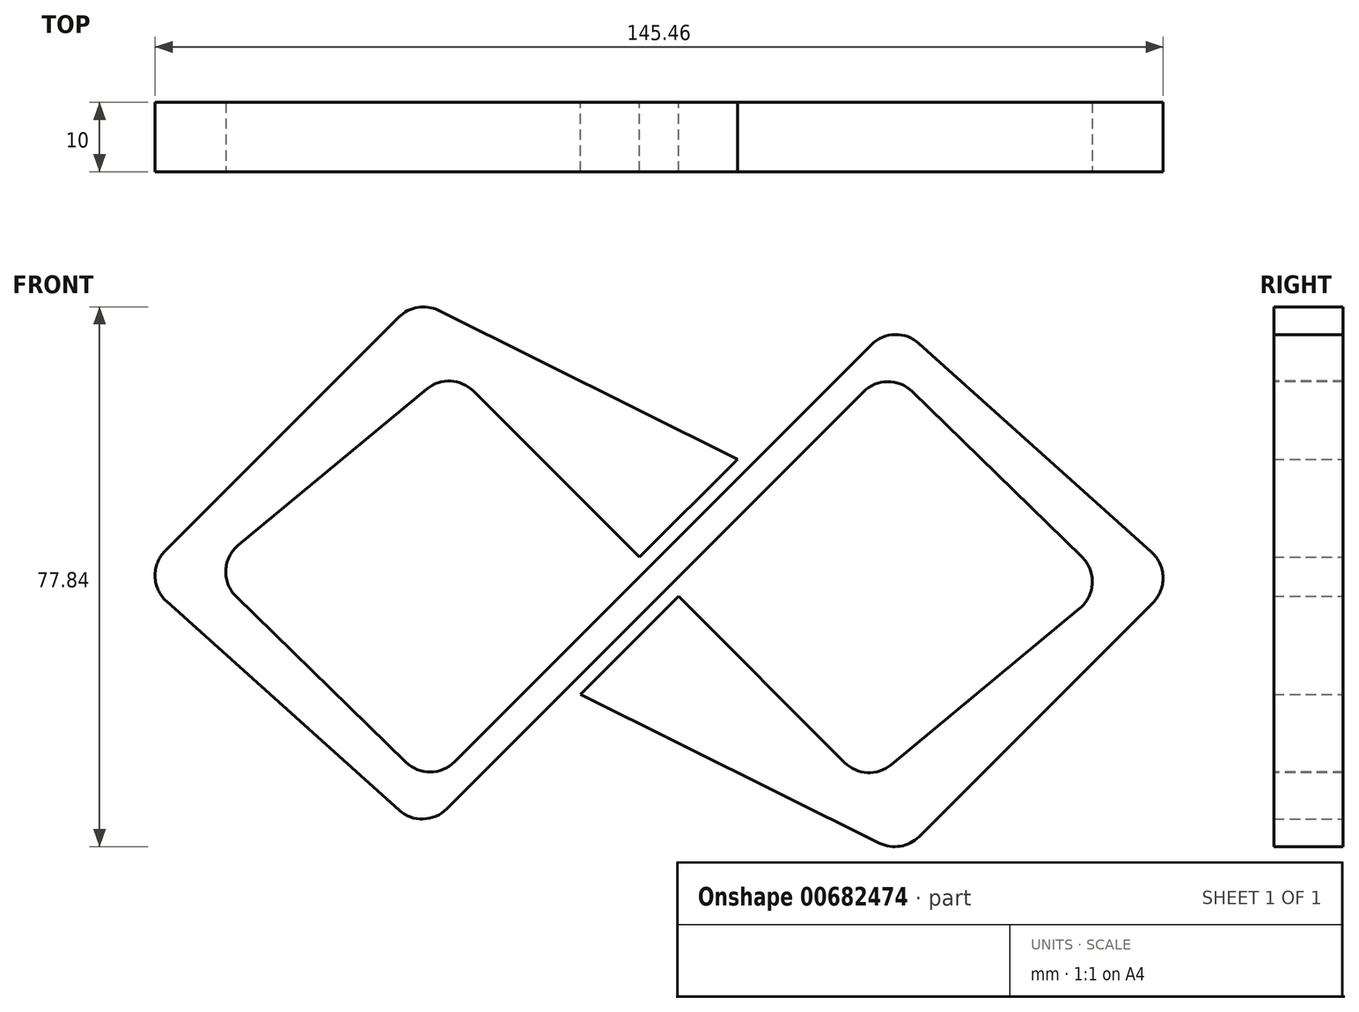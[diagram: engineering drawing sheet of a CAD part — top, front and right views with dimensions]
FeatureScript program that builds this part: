
annotation { "Feature Type Name" : "Feature", "Feature Type Description" : "" }
export const myFeature = defineFeature(function(context is Context, id is Id, definition is map)
    precondition{}
    {
        {
            var Q0;
            Q0=qCreatedBy(makeId("Front.planeOp"),FACE);
            var sketch = newSketch(context, id + "F0", { "sketchPlane" : qUnion([Q0])});
            skLineSegment(sketch, "E0", {"start": v(-34, -36.83) * mm, "end": v(33, 30.17) * mm});
            skLineSegment(sketch, "E1", {"start": v(33, 30.17) * mm, "end": v(65, -1) * mm});
            skLineSegment(sketch, "E2", {"start": v(65, -1) * mm, "end": v(30, -30) * mm});
            skLineSegment(sketch, "E3", {"start": v(30, -30) * mm, "end": v(2.83, -2.83) * mm});
            skLineSegment(sketch, "E4", {"start": v(2.83, -2.83) * mm, "end": v(-11.31, -16.97) * mm});
            skLineSegment(sketch, "E5", {"start": v(-11.31, -16.97) * mm, "end": v(35, -40) * mm});
            skLineSegment(sketch, "E6", {"start": v(35, -40) * mm, "end": v(75, 0) * mm});
            skLineSegment(sketch, "E7", {"start": v(75, 0) * mm, "end": v(34, 36.83) * mm});
            skLineSegment(sketch, "E8", {"start": v(34, 36.83) * mm, "end": v(-33, -30.17) * mm});
            skLineSegment(sketch, "E9", {"start": v(-33, -30.17) * mm, "end": v(-65, 1) * mm});
            skLineSegment(sketch, "E10", {"start": v(-65, 1) * mm, "end": v(-30, 30) * mm});
            skLineSegment(sketch, "E11", {"start": v(-30, 30) * mm, "end": v(-2.83, 2.83) * mm});
            skLineSegment(sketch, "E12", {"start": v(-2.83, 2.83) * mm, "end": v(11.31, 16.97) * mm});
            skLineSegment(sketch, "E13", {"start": v(11.31, 16.97) * mm, "end": v(-35, 40) * mm});
            skLineSegment(sketch, "E14", {"start": v(-35, 40) * mm, "end": v(-75, 0) * mm});
            skLineSegment(sketch, "E15", {"start": v(-75, 0) * mm, "end": v(-34, -36.83) * mm});
            skLineSegment(sketch, "E16", {"start": v(-2.83, 2.83) * mm, "end": v(2.83, -2.83) * mm, "construction": true});
            skSolve(sketch);
        }
        {
            var Q0;
            Q0=makeQuery(id+"F0.imprint","IMPRINT",FACE,{"disambiguationData":[TD([[makeQuery(id+"F0.imprint","IMPRINT",EDGE,{"derivedFrom":sQuery(id+"F0.wireOp",EDGE,"E0")}),1.0]])]});
            extrude(context, id + "F1", {"entities" : qUnion([Q0]), "depth" : 10 * mm, "offsetDistance" : 25 * mm});
        }
        {
            var Q0;
            Q0=makeQuery(id+"F1.opExtrude","SWEPT_EDGE",EDGE,{"disambiguationData":[OSD([sQuery(id+"F0.wireOp",EDGE,"E10"),sQuery(id+"F0.wireOp",EDGE,"E11")])]});
            var Q1;
            Q1=makeQuery(id+"F1.opExtrude","SWEPT_EDGE",EDGE,{"disambiguationData":[OSD([sQuery(id+"F0.wireOp",EDGE,"E9"),sQuery(id+"F0.wireOp",EDGE,"E10")])]});
            var Q2;
            Q2=makeQuery(id+"F1.opExtrude","SWEPT_EDGE",EDGE,{"disambiguationData":[OSD([sQuery(id+"F0.wireOp",EDGE,"E8"),sQuery(id+"F0.wireOp",EDGE,"E9")])]});
            var Q3;
            Q3=makeQuery(id+"F1.opExtrude","SWEPT_EDGE",EDGE,{"disambiguationData":[OSD([sQuery(id+"F0.wireOp",EDGE,"E0"),sQuery(id+"F0.wireOp",EDGE,"E1")])]});
            var Q4;
            Q4=makeQuery(id+"F1.opExtrude","SWEPT_EDGE",EDGE,{"disambiguationData":[OSD([sQuery(id+"F0.wireOp",EDGE,"E1"),sQuery(id+"F0.wireOp",EDGE,"E2")])]});
            var Q5;
            Q5=makeQuery(id+"F1.opExtrude","SWEPT_EDGE",EDGE,{"disambiguationData":[OSD([sQuery(id+"F0.wireOp",EDGE,"E2"),sQuery(id+"F0.wireOp",EDGE,"E3")])]});
            fillet(context, id + "F2", {"entities" : qUnion([Q0, Q1, Q2, Q3, Q4, Q5]), "radius" : 5 * mm, "tangentPropagation" : true, "allowEdgeOverflow" : false});
        }
        {
            var Q0;
            Q0=makeQuery(id+"F1.opExtrude","SWEPT_EDGE",EDGE,{"disambiguationData":[OSD([sQuery(id+"F0.wireOp",EDGE,"E13"),sQuery(id+"F0.wireOp",EDGE,"E14")])]});
            var Q1;
            Q1=makeQuery(id+"F1.opExtrude","SWEPT_EDGE",EDGE,{"disambiguationData":[OSD([sQuery(id+"F0.wireOp",EDGE,"E14"),sQuery(id+"F0.wireOp",EDGE,"E15")])]});
            var Q2;
            Q2=makeQuery(id+"F1.opExtrude","SWEPT_EDGE",EDGE,{"disambiguationData":[OSD([sQuery(id+"F0.wireOp",EDGE,"E0"),sQuery(id+"F0.wireOp",EDGE,"E15")])]});
            var Q3;
            Q3=makeQuery(id+"F1.opExtrude","SWEPT_EDGE",EDGE,{"disambiguationData":[OSD([sQuery(id+"F0.wireOp",EDGE,"E5"),sQuery(id+"F0.wireOp",EDGE,"E6")])]});
            var Q4;
            Q4=makeQuery(id+"F1.opExtrude","SWEPT_EDGE",EDGE,{"disambiguationData":[OSD([sQuery(id+"F0.wireOp",EDGE,"E6"),sQuery(id+"F0.wireOp",EDGE,"E7")])]});
            var Q5;
            Q5=makeQuery(id+"F1.opExtrude","SWEPT_EDGE",EDGE,{"disambiguationData":[OSD([sQuery(id+"F0.wireOp",EDGE,"E7"),sQuery(id+"F0.wireOp",EDGE,"E8")])]});
            fillet(context, id + "F3", {"entities" : qUnion([Q0, Q1, Q2, Q3, Q4, Q5]), "radius" : 5 * mm, "tangentPropagation" : true, "allowEdgeOverflow" : false});
        }
    });
